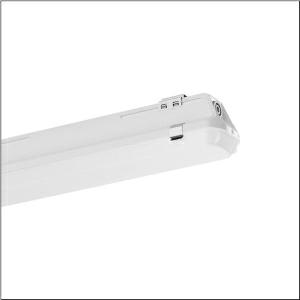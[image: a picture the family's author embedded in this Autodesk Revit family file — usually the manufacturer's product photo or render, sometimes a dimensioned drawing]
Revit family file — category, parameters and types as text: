
# Revit family: monsun_r__21_emergency_51fb10dp468b2_8461
name_source: partatom
category: Lighting Fixtures
units: mm (PartAtom-declared; Revit-internal decimal feet)

## family parameters
Cut with Voids When Loaded = No
Host = Face
Light Source = No
Part Type = Normal
Room Calculation Point = No
Round Connector Dimension = Use Diameter
Shared = No

## types (1)
- --- (1 x LED, 940 lm, 7.3 W, 4000K)
    Apparent Load = 7 VA
    CIE Flux Codes = 47 77 93 94 100
    Color Rendering = 80
    Color Temperature = 4000K
    Default Elevation = 1800 mm
    Description = Monsun® 21 emergency, damp-proof luminaire, chain hanger, primary optical cover: enclosure, of PMMA, light emission: direct distribution, primary light characteristic: symmetric, installation type: suspended mounting, surface-mounted, horizontal mounting, vertical mounting, LED, rated luminous flux: 6.060lm, luminous efficacy: 154lm/W, light colour: 840, colour temperature: 4000K, control gear: ECG DALI, with terminal, 5-pole, max. 2.5mm², mains connection: 220..240V, AC/DC, 0/50..60Hz, rated input power: 39W, housing, of glass-fibre reinforced polyester, uncoated, bright grey, incl. chain hanger, length: 1.590mm, width: 90mm, height: 88mm, clip for enclosure, of stainless steel (V2A), ceiling mounting element, of stainless steel (V2A), chain hanger, of stainless steel (V2A), protection rating (complete): IP66, insulation class (complete): insulation class I (protective earthing), certification: CE, UKCA, protection symbol: D, impact resistance: IK04, permissible operating ambient temperature: -25..+35°C, standard: EN 50419, EN 60598-2-1, EN 60598-2-22, corresponds to IFS (International Featured Standards) requirements for safety and quality in the food industry, for indoor or canopied outdoor use, no direct snow, no direct sun, no direct rain, contact your sales advisor before using the luminaires in applications with unclear chemical exposure, large temperature fluctuations or condensation-forming humidity, LABS conformity tested according to VDMA 24364:2018-05, packaging unit: 1 piece
    Height = 89 mm
    Lamp = 1 x LED
    Lamp Light Flux = 940 lm
    Lamp Power = 7.3 W
    Lamp count = 1
    Length = 1590 mm
    Luminous efficacy = 129 lm/W
    Manufacturer = Siteco
    ModVariant = No
    Model = 51FB10DP468B2
    Mounting Place = Ceiling
    Mounting Type = Surface mounted
    Number of Poles = 1
    OnlyDefault = Yes
    Power Factor = 1
    Product Name = Monsun® 21 emergency
    Product group = damp-proof luminaire
    ProductGroupID = 301
    Protection Class = Protection class I
    Protection Degree = IP 66
    RLX_Detail_Level = 1
    RLX_Emergency_Light_Flux = 0 lm
    RLX_Emergency_Type = 0
    RLX_Emergency_Type_DB = No
    RlxData = <blob elided: 92509 chars, md5=08c12334>
    Socket = socket
    Standby Power = 0 W
    System Light Flux = 940 lm
    System Power = 7 W
    Type Comments = : equivalent power supply (DC)
    Type Image = l_1006717.jpg
    URL = http://relux.com
    VarID = @adj_152081
    Voltage = 0 V
    Weight = 0.00 kg
    Width = 90 mm

## geometry (parser evidence)
native form markers: Blend x4, Sweep x15
no freeform markers — native parametric forms only
